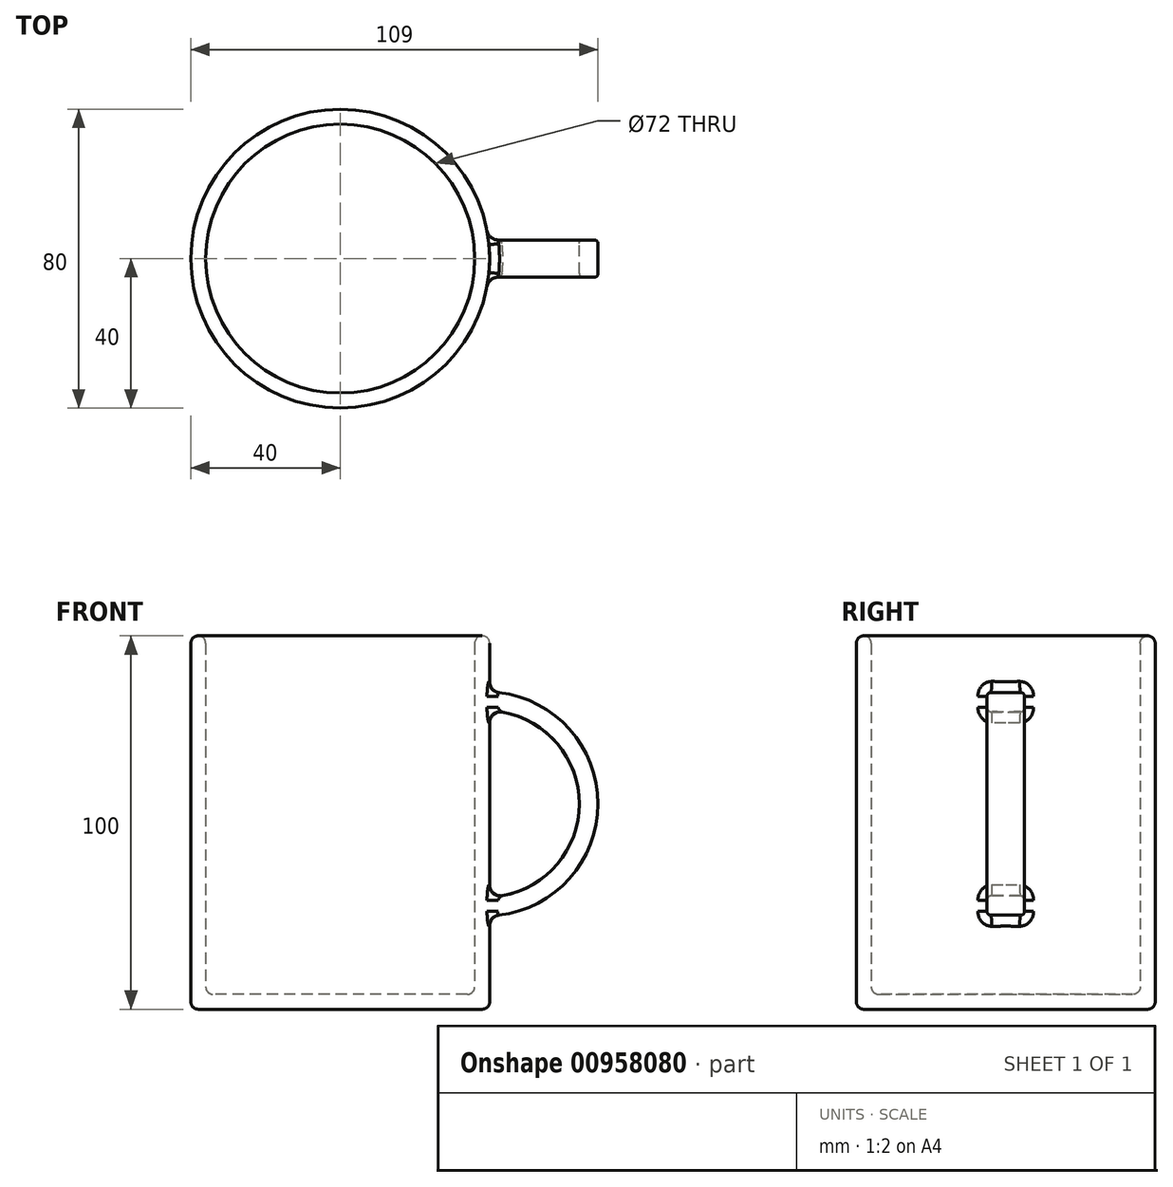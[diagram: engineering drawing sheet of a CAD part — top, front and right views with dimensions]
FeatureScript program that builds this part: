
annotation { "Feature Type Name" : "Feature", "Feature Type Description" : "" }
export const myFeature = defineFeature(function(context is Context, id is Id, definition is map)
    precondition{}
    {
        {
            var Q0;
            Q0=qCreatedBy(makeId("Top.planeOp"),FACE);
            var sketch = newSketch(context, id + "F0", { "sketchPlane" : qUnion([Q0])});
            skCircle(sketch, "E0", {"center": v(0, 0) * mm, "radius": 40 * mm});
            skSolve(sketch);
        }
        {
            var Q0;
            Q0 = qSketchRegion(id + "F0", true);
            extrude(context, id + "F1", {"entities" : qUnion([Q0]), "depth" : 100 * mm, "offsetDistance" : 25 * mm});
        }
        {
            var Q0;
            Q0=makeQuery(id+"F1.opExtrude","CAP_FACE",FACE,{"disambiguationData":[OSD([sQuery(id+"F0.wireOp",EDGE,"E0")])],"isStart":false});
            shell(context, id + "F2", {"entities" : qUnion([Q0]), "thickness" : 4 * mm});
        }
        {
            var Q0;
            Q0=qCreatedBy(makeId("Front.planeOp"),FACE);
            var sketch = newSketch(context, id + "F3", { "sketchPlane" : qUnion([Q0])});
            skArc(sketch, "E1", {"start": v(39, 30) * mm, "mid": v(64, 55) * mm, "end": v(39, 80) * mm});
            skArc(sketch, "E2.0", {"start": v(39, 25) * mm, "mid": v(69, 55) * mm, "end": v(39, 85) * mm});
            skLineSegment(sketch, "E3", {"start": v(39, 80) * mm, "end": v(39, 30) * mm, "construction": true});
            skLineSegment(sketch, "E4", {"start": v(39, 85) * mm, "end": v(39, 80) * mm});
            skLineSegment(sketch, "E5", {"start": v(39, 30) * mm, "end": v(39, 25) * mm});
            skSolve(sketch);
        }
        {
            var Q0;
            Q0 = qSketchRegion(id + "F3", true);
            extrude(context, id + "F4", {"entities" : qUnion([Q0]), "operationType" : NewBodyOperationType.ADD, "depth" : 5 * mm, "offsetDistance" : 25 * mm, "hasSecondDirection" : true, "secondDirectionOppositeDirection" : true, "secondDirectionDepth" : 5 * mm});
        }
        {
            var Q0;
            Q0=makeQuery(id+"F4.opExtrude","CAP_EDGE",EDGE,{"disambiguationData":[OSD([sQuery(id+"F3.wireOp",EDGE,"E2.0")])],"isStart":false});
            var Q1;
            Q1=makeQuery(id+"F4.opExtrude","CAP_EDGE",EDGE,{"disambiguationData":[OSD([sQuery(id+"F3.wireOp",EDGE,"E1")])],"isStart":false});
            var Q2;
            Q2=makeQuery(id+"F4.opExtrude","CAP_EDGE",EDGE,{"disambiguationData":[OSD([sQuery(id+"F3.wireOp",EDGE,"E2.0")])],"isStart":true});
            var Q3;
            Q3=makeQuery(id+"F4.opExtrude","CAP_EDGE",EDGE,{"disambiguationData":[OSD([sQuery(id+"F3.wireOp",EDGE,"E1")])],"isStart":true});
            fillet(context, id + "F5", {"entities" : qUnion([Q0, Q1, Q2, Q3]), "radius" : 1 * mm, "tangentPropagation" : true, "allowEdgeOverflow" : false});
        }
        {
            var Q0;
            Q0=makeQuery(id+"F4.boolean.opBoolean","INTERSECT",EDGE,{"disambiguationData":[OD(1.0)],"derivedFrom":[makeQuery(id+"F1.opExtrude","SWEPT_FACE",FACE,{"disambiguationData":[OSD([sQuery(id+"F0.wireOp",EDGE,"E0")])]}),makeQuery(id+"F4.opExtrude","CAP_FACE",FACE,{"disambiguationData":[OSD([sQuery(id+"F3.wireOp",EDGE,"E1"),sQuery(id+"F3.wireOp",EDGE,"E2.0"),sQuery(id+"F3.wireOp",EDGE,"E4"),sQuery(id+"F3.wireOp",EDGE,"E5")])],"isStart":true})]});
            var Q1;
            Q1=makeQuery(id+"F4.boolean.opBoolean","INTERSECT",EDGE,{"disambiguationData":[OD(0.0)],"derivedFrom":[makeQuery(id+"F1.opExtrude","SWEPT_FACE",FACE,{"disambiguationData":[OSD([sQuery(id+"F0.wireOp",EDGE,"E0")])]}),makeQuery(id+"F4.opExtrude","CAP_FACE",FACE,{"disambiguationData":[OSD([sQuery(id+"F3.wireOp",EDGE,"E1"),sQuery(id+"F3.wireOp",EDGE,"E2.0"),sQuery(id+"F3.wireOp",EDGE,"E4"),sQuery(id+"F3.wireOp",EDGE,"E5")])],"isStart":true})]});
            fillet(context, id + "F6", {"entities" : qUnion([Q0, Q1]), "radius" : 3 * mm, "tangentPropagation" : true, "allowEdgeOverflow" : false});
        }
        {
            var Q0;
            Q0=makeQuery(id+"F1.opExtrude","CAP_FACE",FACE,{"disambiguationData":[OSD([sQuery(id+"F0.wireOp",EDGE,"E0")])],"isStart":false});
            var Q1;
            {var subQ0=sQuery(id+"F0.wireOp",EDGE,"E0");Q1=makeQuery(id+"F2.opShell","OFFSET_EDGE",EDGE,{"disambiguationData":[OSD([subQ0]),TDD([makeQuery(id+"F1.opExtrude","CAP_EDGE",EDGE,{"disambiguationData":[OSD([subQ0])],"isStart":true})])]});}
            var Q2;
            Q2=makeQuery(id+"F1.opExtrude","CAP_EDGE",EDGE,{"disambiguationData":[OSD([sQuery(id+"F0.wireOp",EDGE,"E0")])],"isStart":true});
            fillet(context, id + "F7", {"entities" : qUnion([Q0, Q1, Q2]), "radius" : 2 * mm, "tangentPropagation" : true, "allowEdgeOverflow" : false});
        }
    });
